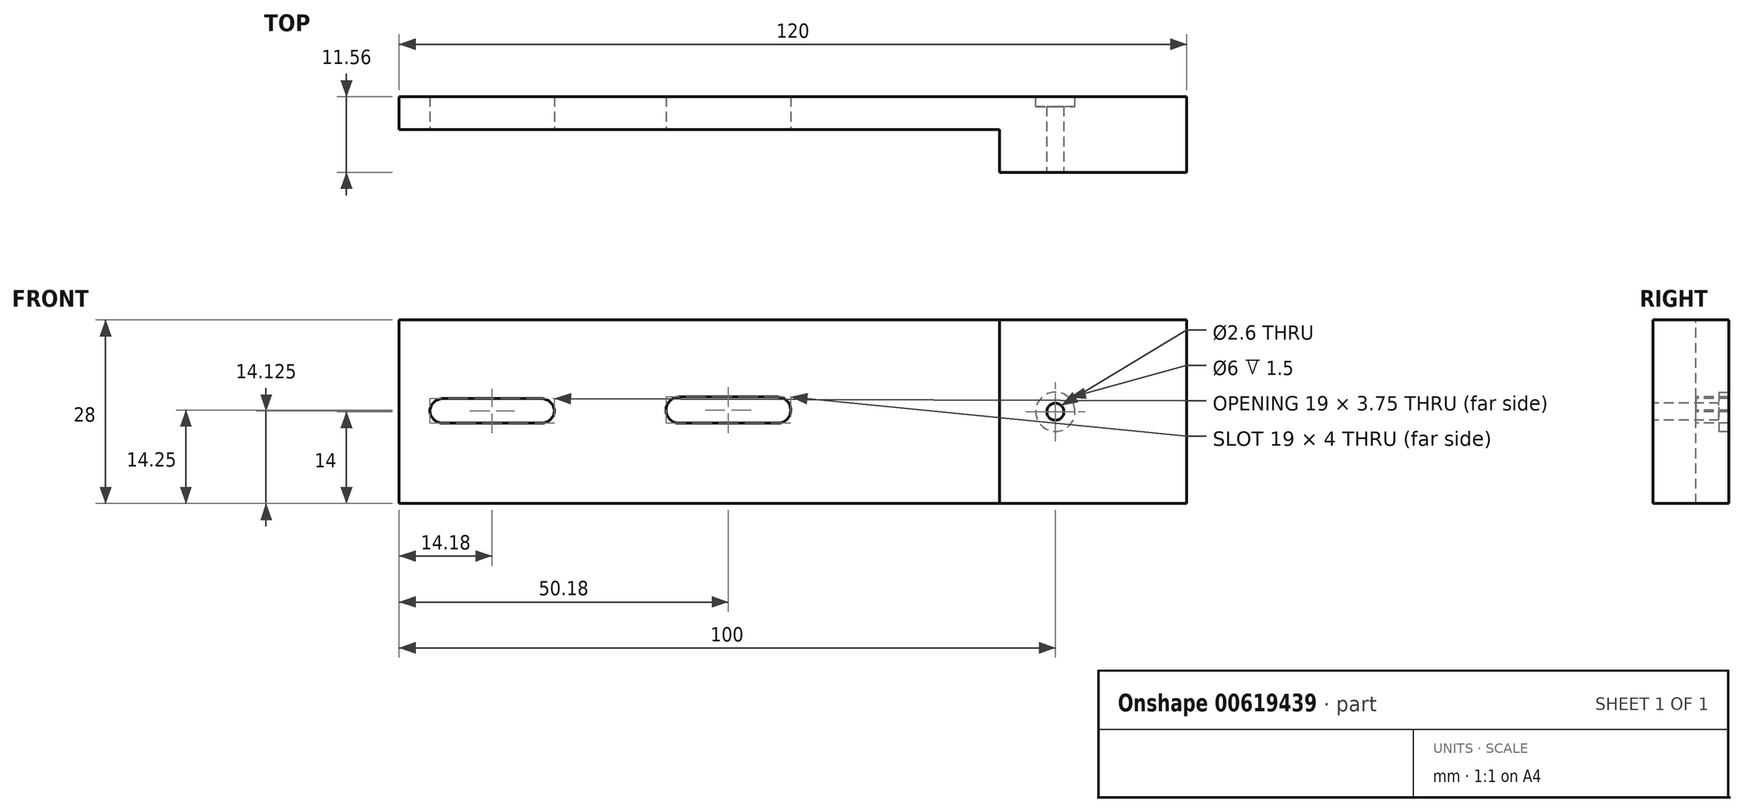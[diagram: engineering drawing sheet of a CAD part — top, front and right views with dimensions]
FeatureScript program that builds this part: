
annotation { "Feature Type Name" : "Feature", "Feature Type Description" : "" }
export const myFeature = defineFeature(function(context is Context, id is Id, definition is map)
    precondition{}
    {
        {
            var Q0;
            Q0=qCreatedBy(makeId("Front.planeOp"),FACE);
            var sketch = newSketch(context, id + "F0", { "sketchPlane" : qUnion([Q0])});
            skLineSegment(sketch, "E0.bottom", {"start": v(0, 0) * mm, "end": v(120, 0) * mm});
            skLineSegment(sketch, "E0.top", {"start": v(0, 28) * mm, "end": v(120, 28) * mm});
            skLineSegment(sketch, "E0.left", {"start": v(0, 0) * mm, "end": v(0, 28) * mm});
            skLineSegment(sketch, "E0.right", {"start": v(120, 0) * mm, "end": v(120, 28) * mm});
            skSolve(sketch);
        }
        {
            var Q0;
            Q0=qSketchRegion(id+"F0",true);
            extrude(context, id + "F1", {"entities" : qUnion([Q0]), "depth" : 5 * mm, "offsetDistance" : 25 * mm});
        }
        {
            var Q0;
            Q0=makeQuery(id+"F1.opExtrude","CAP_FACE",FACE,{"disambiguationData":[OSD([sQuery(id+"F0.wireOp",EDGE,"E0.bottom"),sQuery(id+"F0.wireOp",EDGE,"E0.top"),sQuery(id+"F0.wireOp",EDGE,"E0.left"),sQuery(id+"F0.wireOp",EDGE,"E0.right")])],"isStart":false});
            var sketch = newSketch(context, id + "F2", { "sketchPlane" : qUnion([Q0])});
            skLineSegment(sketch, "E1.bottom", {"start": v(120, 28) * mm, "end": v(91.5, 28) * mm});
            skLineSegment(sketch, "E1.top", {"start": v(120, 0) * mm, "end": v(91.5, 0) * mm});
            skLineSegment(sketch, "E1.left", {"start": v(120, 28) * mm, "end": v(120, 0) * mm});
            skLineSegment(sketch, "E1.right", {"start": v(91.5, 28) * mm, "end": v(91.5, 0) * mm});
            skSolve(sketch);
        }
        {
            var Q0;
            Q0=qSketchRegion(id+"F2",true);
            extrude(context, id + "F3", {"entities" : qUnion([Q0]), "operationType" : NewBodyOperationType.ADD, "depth" : 6.56 * mm, "offsetDistance" : 25 * mm});
        }
        {
            var Q0;
            Q0=makeQuery(id+"F1.opExtrude","CAP_FACE",FACE,{"disambiguationData":[OSD([sQuery(id+"F0.wireOp",EDGE,"E0.bottom"),sQuery(id+"F0.wireOp",EDGE,"E0.top"),sQuery(id+"F0.wireOp",EDGE,"E0.left"),sQuery(id+"F0.wireOp",EDGE,"E0.right")])],"isStart":false});
            var sketch = newSketch(context, id + "F4", { "sketchPlane" : qUnion([Q0])});
            skLineSegment(sketch, "E2", {"start": v(0, 14) * mm, "end": v(107, 14) * mm});
            skLineSegment(sketch, "E3.bottom", {"start": v(57.68, 16.25) * mm, "end": v(42.68, 16.25) * mm});
            skLineSegment(sketch, "E3.top", {"start": v(57.68, 12.25) * mm, "end": v(42.68, 12.25) * mm});
            skLineSegment(sketch, "E3.left", {"start": v(59.68, 14.25) * mm, "end": v(59.68, 14.25) * mm});
            skLineSegment(sketch, "E3.right", {"start": v(40.68, 14.25) * mm, "end": v(40.68, 14.25) * mm});
            skLineSegment(sketch, "E4.bottom", {"start": v(6.68, 16) * mm, "end": v(21.68, 16) * mm});
            skLineSegment(sketch, "E4.top", {"start": v(6.68, 12.25) * mm, "end": v(21.68, 12.25) * mm});
            skLineSegment(sketch, "E4.left", {"start": v(4.68, 14.25) * mm, "end": v(4.68, 14) * mm});
            skLineSegment(sketch, "E4.right", {"start": v(23.68, 14.25) * mm, "end": v(23.68, 14) * mm});
            skPoint(sketch, "E5.visualSharp", {"position": v(40.68, 16.25) * mm});
            skArc(sketch, "E5.filletArc", {"start": v(42.68, 16.25) * mm, "mid": v(41.27, 15.66) * mm, "end": v(40.68, 14.25) * mm});
            skPoint(sketch, "E6.visualSharp", {"position": v(40.68, 12.25) * mm});
            skArc(sketch, "E6.filletArc", {"start": v(40.68, 14.25) * mm, "mid": v(41.27, 12.84) * mm, "end": v(42.68, 12.25) * mm});
            skPoint(sketch, "E7.visualSharp", {"position": v(59.68, 16.25) * mm});
            skArc(sketch, "E7.filletArc", {"start": v(59.68, 14.25) * mm, "mid": v(59.1, 15.66) * mm, "end": v(57.68, 16.25) * mm});
            skPoint(sketch, "E8.visualSharp", {"position": v(59.68, 12.25) * mm});
            skArc(sketch, "E8.filletArc", {"start": v(57.68, 12.25) * mm, "mid": v(59.1, 12.84) * mm, "end": v(59.68, 14.25) * mm});
            skPoint(sketch, "E9.visualSharp", {"position": v(23.68, 16) * mm});
            skArc(sketch, "E9.filletArc", {"start": v(23.68, 14) * mm, "mid": v(23.1, 15.41) * mm, "end": v(21.68, 16) * mm});
            skPoint(sketch, "E10.visualSharp", {"position": v(23.68, 12.25) * mm});
            skArc(sketch, "E10.filletArc", {"start": v(21.68, 12.25) * mm, "mid": v(23.1, 12.84) * mm, "end": v(23.68, 14.25) * mm});
            skPoint(sketch, "E11.visualSharp", {"position": v(4.68, 16) * mm});
            skArc(sketch, "E11.filletArc", {"start": v(6.68, 16) * mm, "mid": v(5.27, 15.41) * mm, "end": v(4.68, 14) * mm});
            skPoint(sketch, "E12.visualSharp", {"position": v(4.68, 12.25) * mm});
            skArc(sketch, "E12.filletArc", {"start": v(4.68, 14.25) * mm, "mid": v(5.27, 12.84) * mm, "end": v(6.68, 12.25) * mm});
            skLineSegment(sketch, "E13", {"start": v(107, 39.5) * mm, "end": v(107, -8.7) * mm});
            skPoint(sketch, "E14.orphan", {"position": v(109.5, 14) * mm});
            skSolve(sketch);
        }
        {
            var Q0;
            Q0=makeQuery(id+"F3.opExtrude","CAP_FACE",FACE,{"disambiguationData":[OSD([sQuery(id+"F2.wireOp",EDGE,"E1.bottom"),sQuery(id+"F2.wireOp",EDGE,"E1.top"),sQuery(id+"F2.wireOp",EDGE,"E1.left"),sQuery(id+"F2.wireOp",EDGE,"E1.right")])],"isStart":false});
            var sketch = newSketch(context, id + "F5", { "sketchPlane" : qUnion([Q0])});
            skCircle(sketch, "E15", {"center": v(100, 14) * mm, "radius": 1.3 * mm});
            skSolve(sketch);
        }
        {
            var Q0;
            Q0=makeQuery(id+"F5.imprint","IMPRINT",FACE,{"disambiguationData":[TD([[makeQuery(id+"F5.imprint","IMPRINT",EDGE,{"derivedFrom":sQuery(id+"F5.wireOp",EDGE,"E15")}),1.0]])]});
            extrude(context, id + "F6", {"entities" : qUnion([Q0]), "operationType" : NewBodyOperationType.REMOVE, "endBound" : BoundingType.UP_TO_NEXT, "oppositeDirection" : true, "depth" : 25 * mm, "offsetDistance" : 25 * mm});
        }
        {
            var Q0;
            Q0=qSketchRegion(id+"F4",true);
            extrude(context, id + "F7", {"entities" : qUnion([Q0]), "operationType" : NewBodyOperationType.REMOVE, "endBound" : BoundingType.UP_TO_NEXT, "oppositeDirection" : true, "depth" : 25 * mm, "offsetDistance" : 25 * mm});
        }
        {
            var Q0;
            Q0=makeQuery(id+"F1.opExtrude","CAP_FACE",FACE,{"disambiguationData":[OSD([sQuery(id+"F0.wireOp",EDGE,"E0.bottom"),sQuery(id+"F0.wireOp",EDGE,"E0.top"),sQuery(id+"F0.wireOp",EDGE,"E0.left"),sQuery(id+"F0.wireOp",EDGE,"E0.right")])],"isStart":true});
            var sketch = newSketch(context, id + "F8", { "sketchPlane" : qUnion([Q0])});
            skCircle(sketch, "E16", {"center": v(-100, 14) * mm, "radius": 3 * mm});
            skSolve(sketch);
        }
        {
            var Q0;
            Q0=makeQuery(id+"F8.imprint","IMPRINT",FACE,{"disambiguationData":[TD([[makeQuery(id+"F8.imprint","IMPRINT",EDGE,{"derivedFrom":sQuery(id+"F8.wireOp",EDGE,"E16")}),1.0]])]});
            extrude(context, id + "F9", {"entities" : qUnion([Q0]), "operationType" : NewBodyOperationType.REMOVE, "oppositeDirection" : true, "depth" : 1.5 * mm, "offsetDistance" : 25 * mm});
        }
    });
